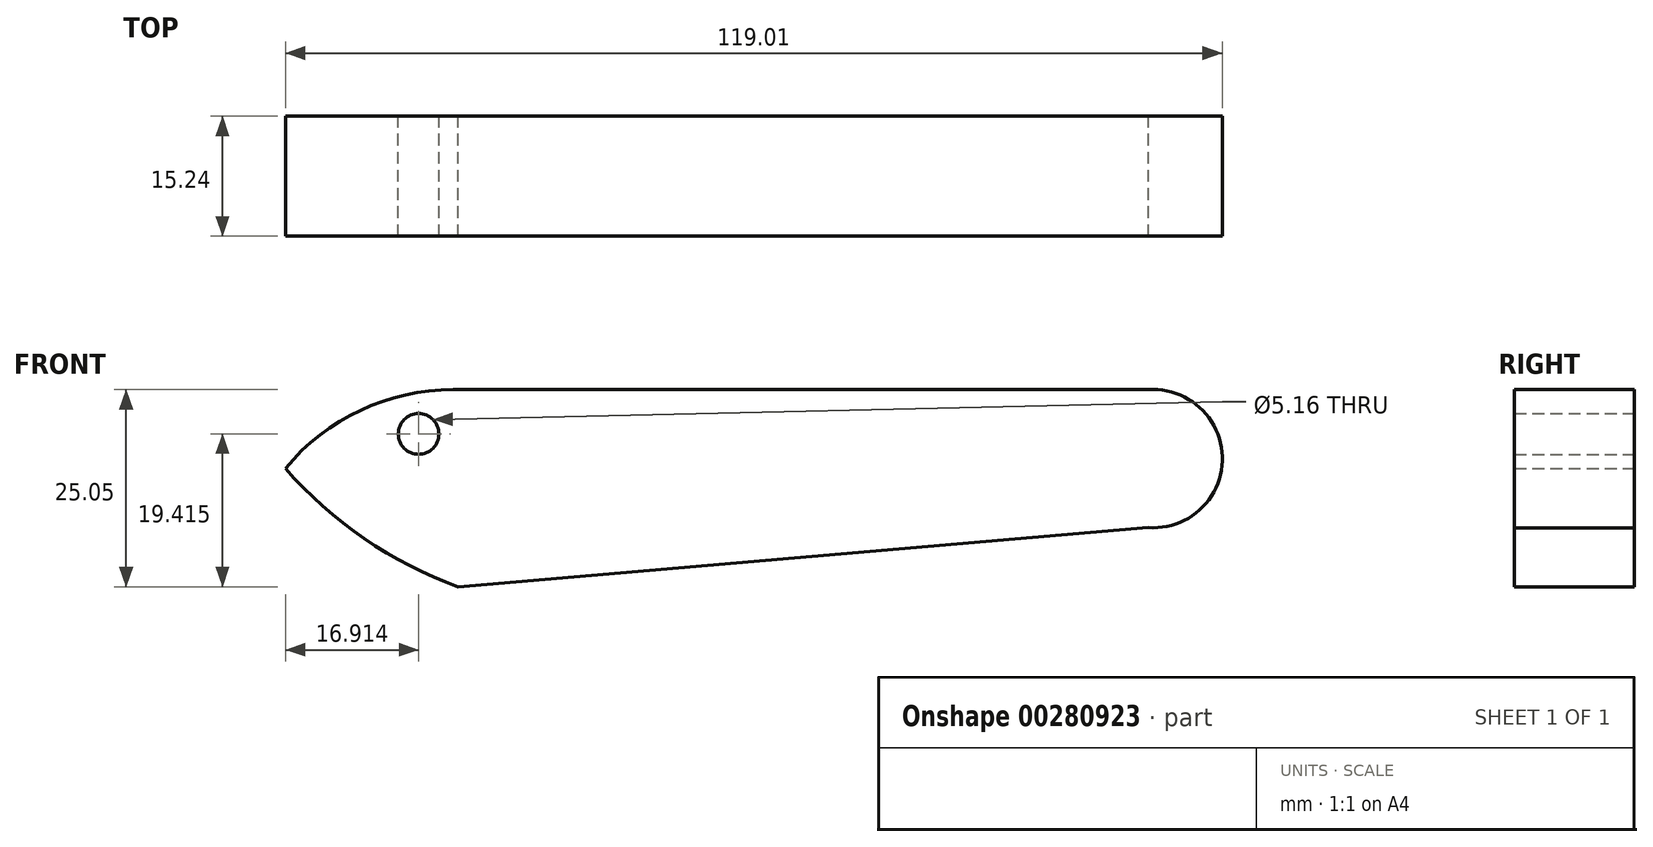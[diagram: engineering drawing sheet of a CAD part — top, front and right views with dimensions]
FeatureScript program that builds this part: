
annotation { "Feature Type Name" : "Feature", "Feature Type Description" : "" }
export const myFeature = defineFeature(function(context is Context, id is Id, definition is map)
    precondition{}
    {
        {
            var Q0;
            Q0=qCreatedBy(makeId("Front.planeOp"),FACE);
            var sketch = newSketch(context, id + "F0", { "sketchPlane" : qUnion([Q0])});
            skLineSegment(sketch, "E0", {"start": v(-53.86, 13.62) * mm, "end": v(35.07, 13.62) * mm});
            skArc(sketch, "E1", {"start": v(-53.86, 13.62) * mm, "mid": v(-65.63, 11) * mm, "end": v(-75.16, 3.6) * mm});
            skLineSegment(sketch, "E2", {"start": v(-53.24, -11.43) * mm, "end": v(34.45, -3.91) * mm});
            skArc(sketch, "E3", {"start": v(-75.16, 3.6) * mm, "mid": v(-65.14, -5.3) * mm, "end": v(-53.24, -11.43) * mm});
            skArc(sketch, "E4", {"start": v(34.45, -3.91) * mm, "mid": v(43.85, 4.53) * mm, "end": v(35.07, 13.62) * mm});
            skCircle(sketch, "E5", {"center": v(-58.25, 7.99) * mm, "radius": 2.58 * mm});
            skSolve(sketch);
        }
        {
            var Q0;
            Q0 = qSketchRegion(id + "F0", true);
            extrude(context, id + "F1", {"entities" : qUnion([Q0]), "depth" : 15.24 * mm});
        }
    });
